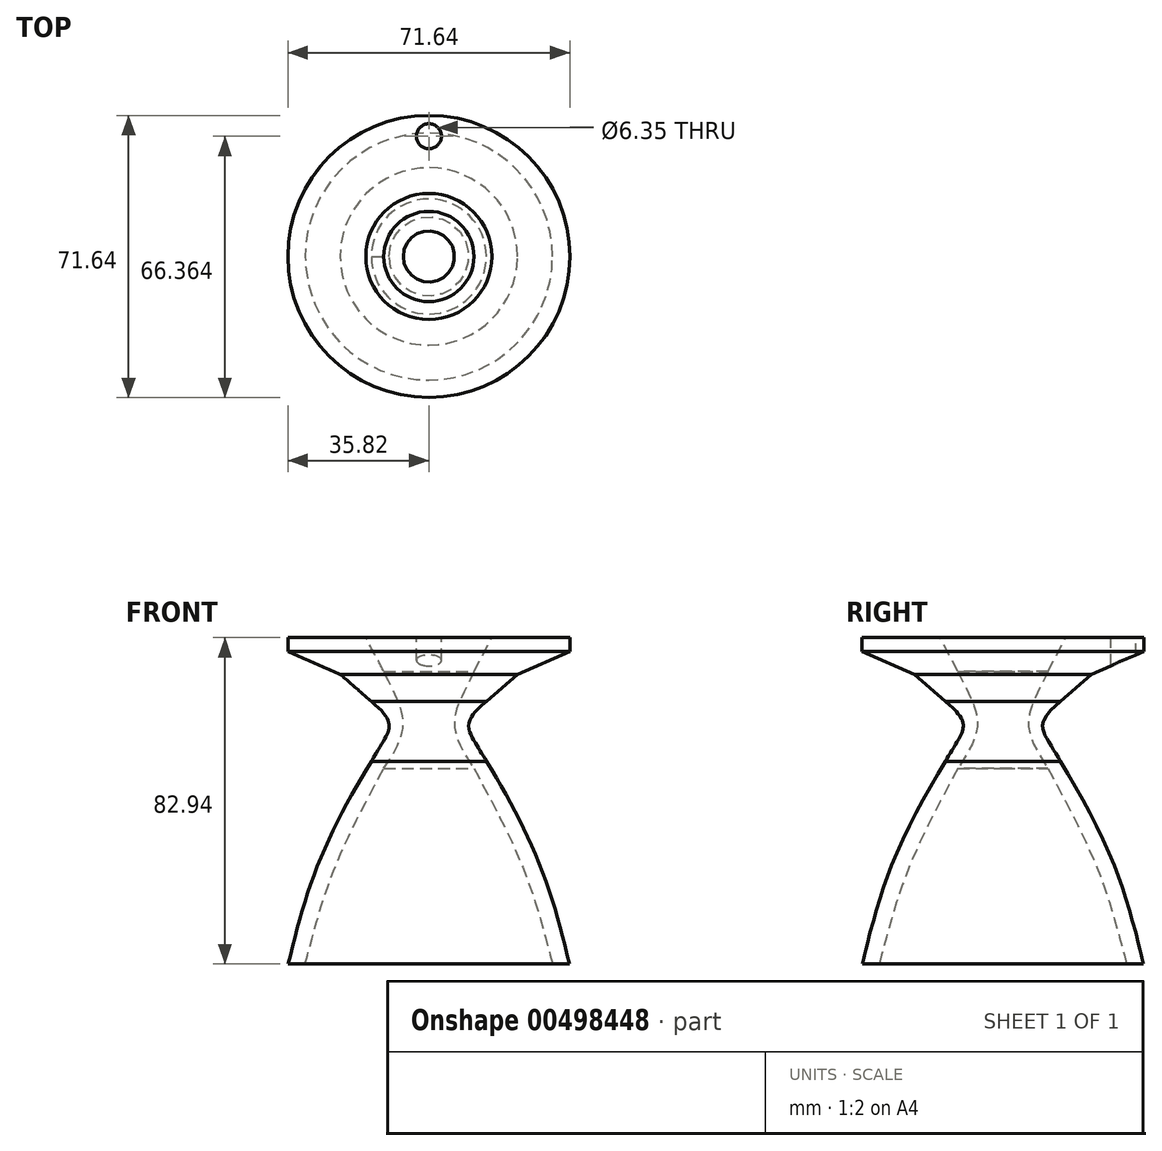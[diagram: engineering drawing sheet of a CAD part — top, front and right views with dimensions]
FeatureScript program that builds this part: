
annotation { "Feature Type Name" : "Feature", "Feature Type Description" : "" }
export const myFeature = defineFeature(function(context is Context, id is Id, definition is map)
    precondition{}
    {
        {
            var Q0;
            Q0=qCreatedBy(makeId("Front.planeOp"),FACE);
            var sketch = newSketch(context, id + "F0", { "sketchPlane" : qUnion([Q0])});
            skLineSegment(sketch, "E0", {"start": v(0, -9.82) * mm, "end": v(0, 22.74) * mm});
            skLineSegment(sketch, "E1", {"start": v(-35.71, 0) * mm, "end": v(-31.4, 0) * mm});
            skFitSpline(sketch, "E2", {"points": [v(-35.71, 0) * mm, v(-28.2, 25.17) * mm, v(-14.61, 51.47) * mm], "startDerivative": vector(12.45, 51.8) * mm, "endDerivative": vector(29.31, 47.08) * mm});
            skFitSpline(sketch, "E3", {"points": [v(-14.61, 51.47) * mm, v(-10.13, 59.83) * mm, v(-14.61, 66.69) * mm], "startDerivative": vector(13.99, 25.1) * mm, "endDerivative": vector(-24.2, 19.84) * mm});
            skFitSpline(sketch, "E4", {"points": [v(-31.4, 0) * mm, v(-24.15, 23.8) * mm, v(-11.46, 49.67) * mm], "startDerivative": vector(12.77, 49.3) * mm, "endDerivative": vector(26.93, 50.03) * mm});
            skFitSpline(sketch, "E5", {"points": [v(-11.46, 49.67) * mm, v(-6.5, 61.08) * mm, v(-11.46, 74.33) * mm], "startDerivative": vector(13.93, 20.37) * mm, "endDerivative": vector(-13.13, 28.71) * mm});
            skLineSegment(sketch, "E6", {"start": v(-11.46, 74.33) * mm, "end": v(-16.02, 82.94) * mm});
            skLineSegment(sketch, "E7", {"start": v(-16.02, 82.94) * mm, "end": v(-35.82, 82.94) * mm});
            skLineSegment(sketch, "E8", {"start": v(-35.82, 82.94) * mm, "end": v(-35.82, 79.41) * mm});
            skLineSegment(sketch, "E9", {"start": v(-22.53, 73.62) * mm, "end": v(-14.61, 66.69) * mm});
            skLineSegment(sketch, "E10", {"start": v(-22.53, 73.62) * mm, "end": v(-35.82, 79.41) * mm});
            skSolve(sketch);
        }
        {
            var Q0;
            Q0=makeQuery(id+"F0.imprint","IMPRINT",FACE,{"disambiguationData":[TD([[makeQuery(id+"F0.imprint","IMPRINT",EDGE,{"derivedFrom":sQuery(id+"F0.wireOp",EDGE,"E1")}),1.0]])]});
            var Q1;
            Q1=sQuery(id+"F0.wireOp",EDGE,"E0");
            revolve(context, id + "F1", {"entities" : qUnion([Q0]), "axis" : qUnion([Q1]), "revolveType" : RevolveType.FULL});
        }
        {
            var Q0;
            Q0=makeQuery(id+"F1.opRevolve","SWEPT_FACE",FACE,{"disambiguationData":[OSD([sQuery(id+"F0.wireOp",EDGE,"E7")])]});
            var sketch = newSketch(context, id + "F2", { "sketchPlane" : qUnion([Q0])});
            skSolve(sketch);
        }
        {
            var Q0;
            {var subQ0=sQuery(id+"F0.wireOp",EDGE,"E7");Q0=makeQuery(id+"F2.imprint","IMPRINT",FACE,{"disambiguationData":[TD([[makeQuery(id+"F2.imprint","IMPRINT",EDGE,{"derivedFrom":makeQuery(id+"F1.opRevolve","SWEPT_EDGE",EDGE,{"disambiguationData":[OSD([sQuery(id+"F0.wireOp",EDGE,"E6"),subQ0])]})}),1.0]])]});}
            var sketch = newSketch(context, id + "F3", { "sketchPlane" : qUnion([Q0])});
            skCircle(sketch, "E11", {"center": v(0, 30.54) * mm, "radius": 2.5 * mm});
            skSolve(sketch);
        }
        {
            var Q0;
            Q0=sQuery(id+"F3.wireOp",VERTEX,"E11.center");
            var Q1;
            Q1=makeQuery(id+"F1.opRevolve","SWEPT_BODY",BODY,{"disambiguationData":[OSD([sQuery(id+"F0.wireOp",EDGE,"E1"),sQuery(id+"F0.wireOp",EDGE,"E2"),sQuery(id+"F0.wireOp",EDGE,"E3"),sQuery(id+"F0.wireOp",EDGE,"E4"),sQuery(id+"F0.wireOp",EDGE,"E5"),sQuery(id+"F0.wireOp",EDGE,"E6"),sQuery(id+"F0.wireOp",EDGE,"E7"),sQuery(id+"F0.wireOp",EDGE,"E8"),sQuery(id+"F0.wireOp",EDGE,"Lme2o6aa-KmSF-zKBj-fWwe-3R7ETdqKsuKE"),sQuery(id+"F0.wireOp",EDGE,"zatWymTD-embI-ejKd-GjeW-QvA4nIx3lMoH"),sQuery(id+"F0.wireOp",EDGE,"E9")])]});
            hole(context, id + "F4", {"style" : HoleStyle.SIMPLE, "endStyle" : HoleEndStyle.BLIND, "holeDiameter" : 6.35 * mm, "holeDepth" : 12.7 * mm, "tappedDepth" : 12.7 * mm, "tapClearance" : 3, "locations" : qUnion([Q0]), "scope" : qUnion([Q1])});
        }
    });
